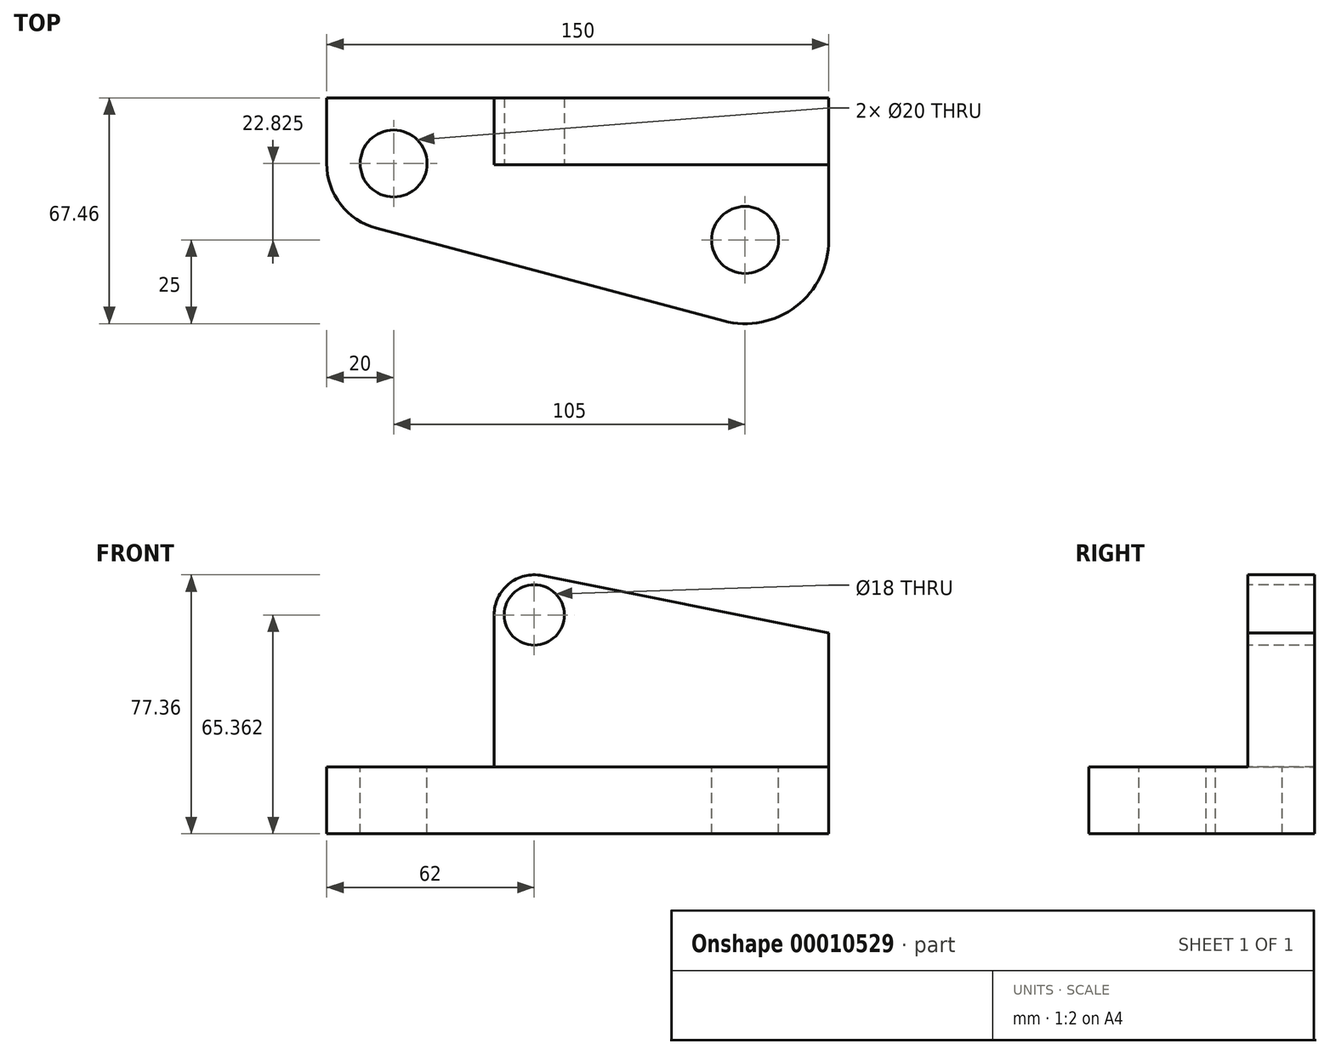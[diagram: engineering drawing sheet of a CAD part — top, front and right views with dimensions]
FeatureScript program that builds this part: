
annotation { "Feature Type Name" : "Feature", "Feature Type Description" : "" }
export const myFeature = defineFeature(function(context is Context, id is Id, definition is map)
    precondition{}
    {
        {
            var Q0;
            Q0=qCreatedBy(makeId("Top.planeOp"),FACE);
            var sketch = newSketch(context, id + "F0", { "sketchPlane" : qUnion([Q0])});
            skLineSegment(sketch, "E0", {"start": v(0, 0) * mm, "end": v(-150, 0) * mm});
            skLineSegment(sketch, "E1", {"start": v(-150, 0) * mm, "end": v(-150, -35) * mm});
            skLineSegment(sketch, "E2", {"start": v(-150, -35) * mm, "end": v(0, -75) * mm});
            skLineSegment(sketch, "E3", {"start": v(0, -75) * mm, "end": v(0, 0) * mm});
            skSolve(sketch);
        }
        {
            var Q0;
            Q0 = qSketchRegion(id + "F0", true);
            extrude(context, id + "F1", {"entities" : qUnion([Q0]), "depth" : 20 * mm});
        }
        {
            var Q0;
            Q0=qCreatedBy(makeId("Front.planeOp"),FACE);
            var sketch = newSketch(context, id + "F2", { "sketchPlane" : qUnion([Q0])});
            skLineSegment(sketch, "E4", {"start": v(0, 0) * mm, "end": v(0, 60) * mm});
            skLineSegment(sketch, "E5", {"start": v(0, 60) * mm, "end": v(-100, 80) * mm});
            skLineSegment(sketch, "E6", {"start": v(-100, 80) * mm, "end": v(-100, 0) * mm});
            skLineSegment(sketch, "E7", {"start": v(-100, 0) * mm, "end": v(0, 0) * mm});
            skSolve(sketch);
        }
        {
            var Q0;
            Q0 = qSketchRegion(id + "F2", true);
            extrude(context, id + "F3", {"entities" : qUnion([Q0]), "operationType" : NewBodyOperationType.ADD, "depth" : 20 * mm});
        }
        {
            var Q0;
            Q0=makeQuery(id+"F1.opExtrude","SWEPT_EDGE",EDGE,{"disambiguationData":[OSD([sQuery(id+"F0.wireOp",EDGE,"E1"),sQuery(id+"F0.wireOp",EDGE,"E2")])]});
            fillet(context, id + "F4", {"entities" : qUnion([Q0]), "radius" : 20 * mm, "tangentPropagation" : true, "allowEdgeOverflow" : false});
        }
        {
            var Q0;
            Q0=makeQuery(id+"F1.opExtrude","SWEPT_EDGE",EDGE,{"disambiguationData":[OSD([sQuery(id+"F0.wireOp",EDGE,"E2"),sQuery(id+"F0.wireOp",EDGE,"E3")])]});
            fillet(context, id + "F5", {"entities" : qUnion([Q0]), "radius" : 25 * mm, "tangentPropagation" : true, "allowEdgeOverflow" : false});
        }
        {
            var Q0;
            Q0=makeQuery(id+"F3.opExtrude","SWEPT_EDGE",EDGE,{"disambiguationData":[OSD([sQuery(id+"F2.wireOp",EDGE,"E5"),sQuery(id+"F2.wireOp",EDGE,"E6")])]});
            fillet(context, id + "F6", {"entities" : qUnion([Q0]), "radius" : 12 * mm, "tangentPropagation" : true, "allowEdgeOverflow" : false});
        }
        {
            var Q0;
            Q0=makeQuery(id+"F1.opExtrude","CAP_FACE",FACE,{"disambiguationData":[OSD([sQuery(id+"F0.wireOp",EDGE,"E0"),sQuery(id+"F0.wireOp",EDGE,"E1"),sQuery(id+"F0.wireOp",EDGE,"E2"),sQuery(id+"F0.wireOp",EDGE,"E3")])],"isStart":false});
            var sketch = newSketch(context, id + "F7", { "sketchPlane" : qUnion([Q0])});
            skCircle(sketch, "E8", {"center": v(-130, -19.63) * mm, "radius": 10 * mm});
            skCircle(sketch, "E9", {"center": v(-25, -42.46) * mm, "radius": 10 * mm});
            skSolve(sketch);
        }
        {
            var Q0;
            Q0 = qSketchRegion(id + "F7", true);
            extrude(context, id + "F8", {"entities" : qUnion([Q0]), "operationType" : NewBodyOperationType.REMOVE, "endBound" : BoundingType.THROUGH_ALL, "oppositeDirection" : true, "depth" : 25 * mm});
        }
        {
            var Q0;
            Q0=makeQuery(id+"F3.opExtrude","CAP_FACE",FACE,{"disambiguationData":[OSD([sQuery(id+"F2.wireOp",EDGE,"E4"),sQuery(id+"F2.wireOp",EDGE,"E5"),sQuery(id+"F2.wireOp",EDGE,"E6"),sQuery(id+"F2.wireOp",EDGE,"E7")])],"isStart":false});
            var sketch = newSketch(context, id + "F9", { "sketchPlane" : qUnion([Q0])});
            skCircle(sketch, "E10", {"center": v(-88, 65.36) * mm, "radius": 9 * mm});
            skSolve(sketch);
        }
        {
            var Q0;
            Q0 = qSketchRegion(id + "F9", true);
            extrude(context, id + "F10", {"entities" : qUnion([Q0]), "operationType" : NewBodyOperationType.REMOVE, "endBound" : BoundingType.THROUGH_ALL, "oppositeDirection" : true, "depth" : 25 * mm});
        }
    });
